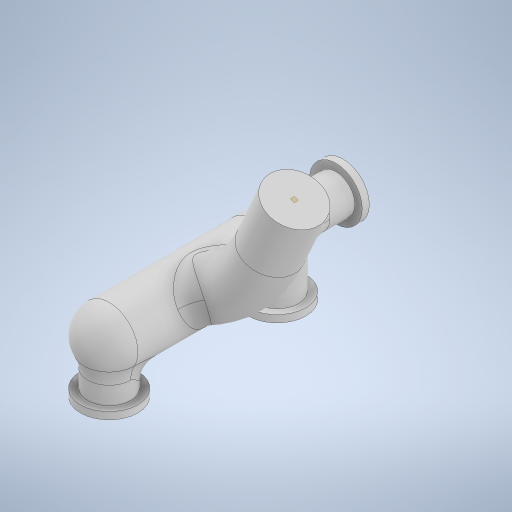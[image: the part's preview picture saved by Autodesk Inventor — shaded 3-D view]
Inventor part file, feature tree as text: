
AUTODESK INVENTOR PART (.ipt)
format: ipt  version: 2023 (Build 270158000, 158)  size: 620,032 bytes
history: native  units: in
note: dims shown in document units (in); Inventor stores cm internally (conversion verified against a paired STEP export)
features: sketch x7, extrude x5, fillet x3, other x2, plane x2, revolve x1, loft x1, sweep x1, mirror x1, projected_geometry x1
ambient origin geometry x8: Origin, YZ Plane, XZ Plane, XY Plane, X Axis, Y Axis, Z Axis, Center Point
bodies: Solid1 (feature_tree)
feature tree (24):
  other  "intake_manifold_f"
  revolve  "Revolution1"  [1 undecoded]
  plane  "Work Plane1"
  loft  "Loft1"
  extrude  "Extrusion1"  Depth=2.0in
  fillet  "Fillet1"  Radius=0.3937in
  extrude  "Extrusion2"  Depth=9.0in
  extrude  "Extrusion3"  Depth=11.0in TaperAngle=0.0deg
  extrude  "Extrusion4"  Depth=12.0in
  sketch  "Sketch9"  dims[d20=12.0in d21=12.0in]
  plane  "Work Plane2"
  sweep  "Sweep2"
  fillet  "Fillet5"  Radius=1.0in
  extrude  "Extrusion6"  Depth=8.0in
  fillet  "Fillet6"  Radius=5.25in
  mirror  "Mirror3"
  sketch  "Sketch3"  dims[d3=30.0in d4=6.0in]
  other  "Edges1"
  sketch  "Sketch4"  dims[d5=90.0deg d6=12.0in]
  sketch  "Sketch5"  dims[d7=8.0in d8=2.0in d9=0.3937in d10=90.0deg]
  projected_geometry  "Projected Loop1"
  sketch  "Sketch6"  dims[d13=0.3937in d14=90.0deg d15=9.0in]
  sketch  "Sketch7"  dims[d16=9.0in d17=11.0in d18=0.0in]
  sketch  "Sketch10"  dims[d22=1.5in d23=0.0in d24=6.0in d25=6.0in d26=6.0in d27=0.0in d28=2.0in d29=0.1969in d30=6.0in d31=0.3937in d33=1.0in d34=0.0in d35=8.0in d36=5.25in d37=0.0in d52=11.0in d56=0.0in d57=0.0in d58=3.0in d59=0.0in d60=5.0in d61=11.0in d62=1.5in d63=0.0in d64=3.0in d65=3.0in d66=3.0in d67=0.0in d68=2.0in d69=0.1291in d70=3.0in d71=0.2583in d72=2.0in d73=0.326in d74=2.5in]
note: 1 required parameter value undecoded (feature->parameter linkage not recoverable at this tier; creation-order binding heuristic only, values carry confidence <= 0.55)
